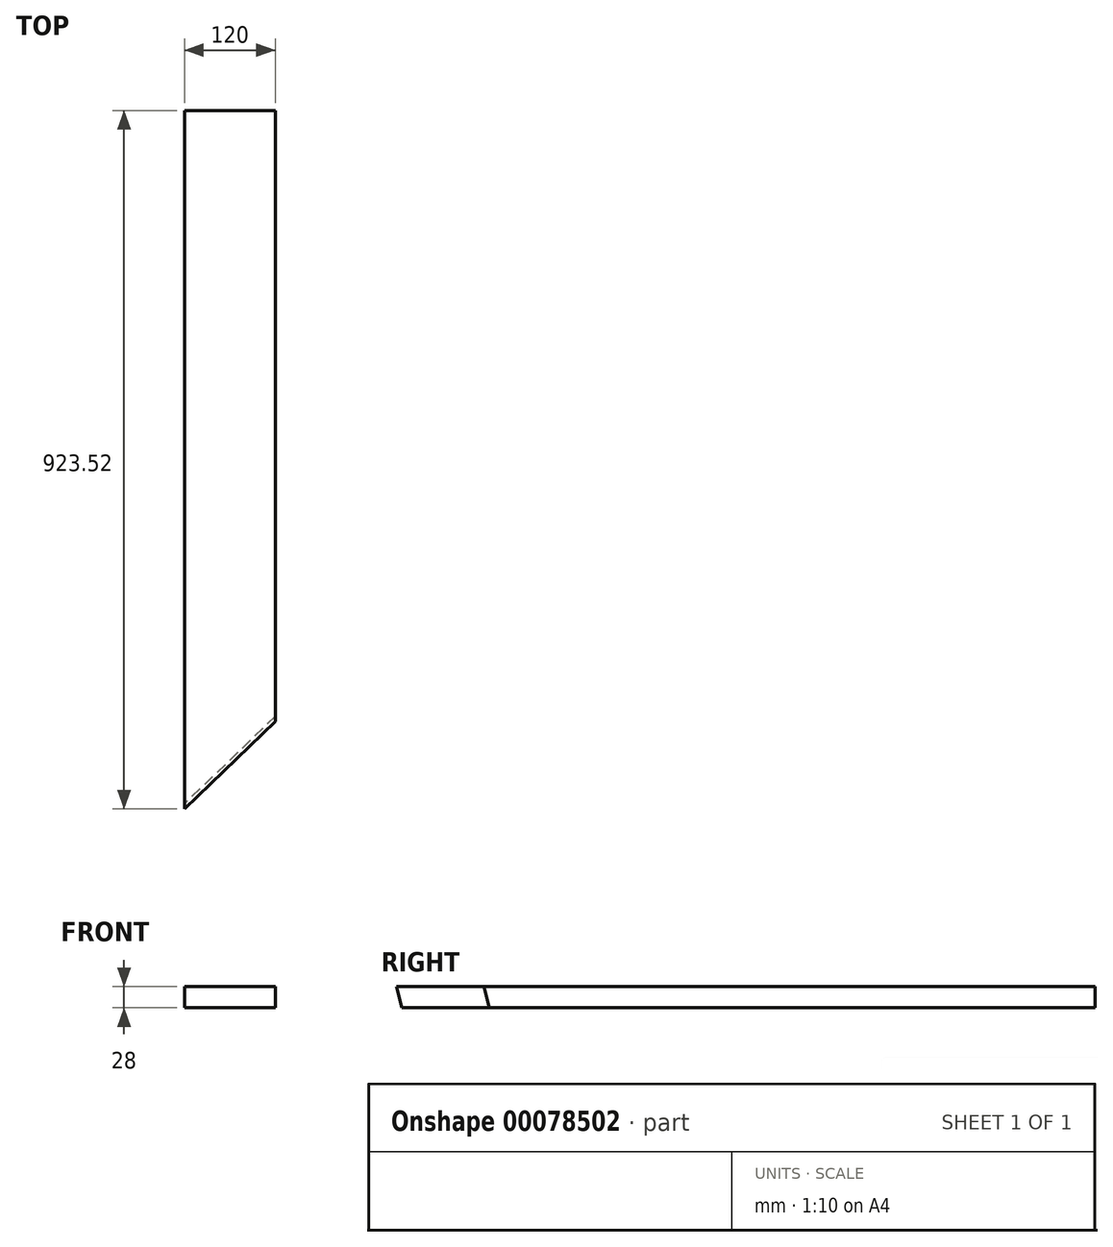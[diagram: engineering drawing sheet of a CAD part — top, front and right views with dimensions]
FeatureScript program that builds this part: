
annotation { "Feature Type Name" : "Feature", "Feature Type Description" : "" }
export const myFeature = defineFeature(function(context is Context, id is Id, definition is map)
    precondition{}
    {
        {
            var Q0;
            Q0=qCreatedBy(makeId("Front.planeOp"),FACE);
            var sketch = newSketch(context, id + "F0", { "sketchPlane" : qUnion([Q0])});
            skLineSegment(sketch, "E0.bottom", {"start": v(60, -14) * mm, "end": v(-60, -14) * mm});
            skLineSegment(sketch, "E0.top", {"start": v(60, 14) * mm, "end": v(-60, 14) * mm});
            skLineSegment(sketch, "E0.left", {"start": v(60, -14) * mm, "end": v(60, 14) * mm});
            skLineSegment(sketch, "E0.right", {"start": v(-60, -14) * mm, "end": v(-60, 14) * mm});
            skPoint(sketch, "E0.middle", {"position": v(0, 0) * mm});
            skSolve(sketch);
        }
        {
            var Q0;
            Q0=makeQuery(id+"F0.imprint","IMPRINT",FACE,{"disambiguationData":[TD([[makeQuery(id+"F0.imprint","IMPRINT",EDGE,{"derivedFrom":sQuery(id+"F0.wireOp",EDGE,"E0.bottom")}),-1.0]])]});
            extrude(context, id + "F1", {"entities" : qUnion([Q0]), "endBound" : BoundingType.SYMMETRIC, "depth" : 925 * mm});
        }
        {
            var Q0;
            Q0=makeQuery(id+"F1.opExtrude","CAP_EDGE",EDGE,{"disambiguationData":[OSD([sQuery(id+"F0.wireOp",EDGE,"E0.left")])],"isStart":false});
            chamfer(context, id + "F2", {"entities" : qUnion([Q0]), "chamferType" : ChamferType.OFFSET_ANGLE, "width" : 120 * mm, "oppositeDirection" : false, "angle" : 44 * degree, "tangentPropagation" : true});
        }
        {
            var Q0;
            Q0=makeQuery(id+"F2.opChamfer","BLEND_EDGE",EDGE,{"blendedFrom":[makeQuery(id+"F1.opExtrude","CAP_EDGE",EDGE,{"disambiguationData":[OSD([sQuery(id+"F0.wireOp",EDGE,"E0.left")])],"isStart":false}),makeQuery(id+"F1.opExtrude","SWEPT_FACE",FACE,{"disambiguationData":[OSD([sQuery(id+"F0.wireOp",EDGE,"E0.bottom")])]})],"blendedInto":[makeQuery(id+"F1.opExtrude","SWEPT_FACE",FACE,{"disambiguationData":[OSD([sQuery(id+"F0.wireOp",EDGE,"E0.bottom")])]})]});
            chamfer(context, id + "F3", {"entities" : qUnion([Q0]), "chamferType" : ChamferType.OFFSET_ANGLE, "width" : 6 * mm, "oppositeDirection" : false, "angle" : 80 * degree, "tangentPropagation" : true});
        }
    });
